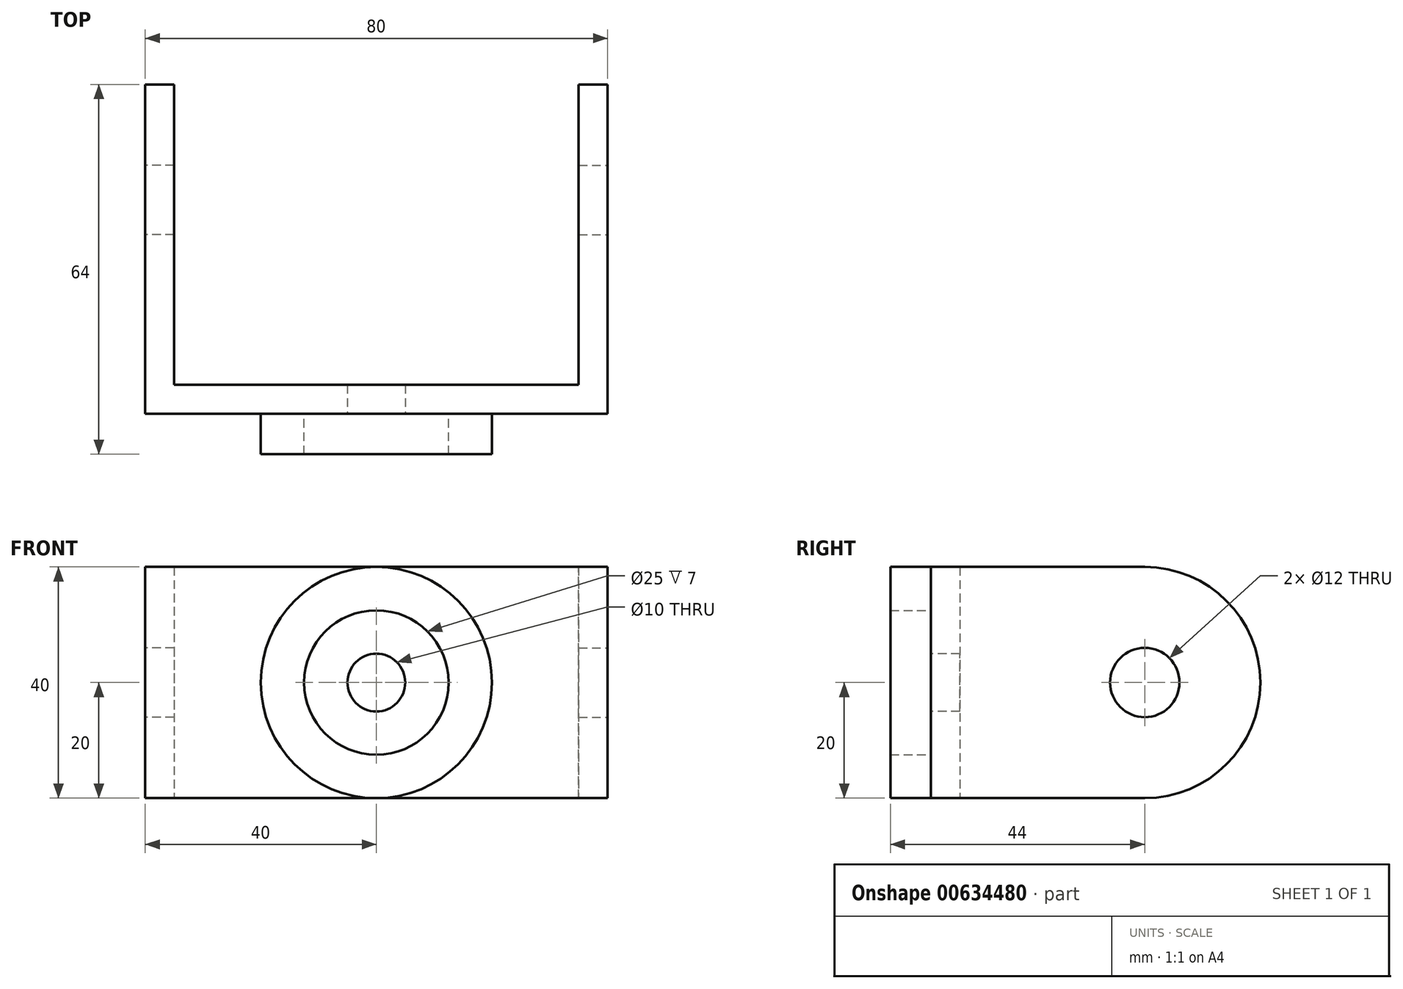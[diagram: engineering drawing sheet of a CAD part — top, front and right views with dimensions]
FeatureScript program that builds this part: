
annotation { "Feature Type Name" : "Feature", "Feature Type Description" : "" }
export const myFeature = defineFeature(function(context is Context, id is Id, definition is map)
    precondition{}
    {
        {
            var Q0;
            Q0=qCreatedBy(makeId("Front.planeOp"),FACE);
            var sketch = newSketch(context, id + "F0", { "sketchPlane" : qUnion([Q0])});
            skLineSegment(sketch, "E0.bottom", {"start": v(40, 20) * mm, "end": v(-40, 20) * mm});
            skLineSegment(sketch, "E0.top", {"start": v(40, -20) * mm, "end": v(-40, -20) * mm});
            skLineSegment(sketch, "E0.left", {"start": v(40, 20) * mm, "end": v(40, -20) * mm});
            skLineSegment(sketch, "E0.right", {"start": v(-40, 20) * mm, "end": v(-40, -20) * mm});
            skPoint(sketch, "E0.middle", {"position": v(0, 0) * mm});
            skCircle(sketch, "E1", {"center": v(0, 0) * mm, "radius": 5 * mm});
            skCircle(sketch, "E2", {"center": v(0, 0) * mm, "radius": 12.5 * mm});
            skCircle(sketch, "E3", {"center": v(0, 0) * mm, "radius": 20 * mm});
            skSolve(sketch);
        }
        {
            var Q0;
            Q0=makeQuery(id+"F0.imprint","IMPRINT",FACE,{"disambiguationData":[TD([[makeQuery(id+"F0.imprint","IMPRINT",EDGE,{"derivedFrom":sQuery(id+"F0.wireOp",EDGE,"E2")}),-1.0]])]});
            extrude(context, id + "F1", {"entities" : qUnion([Q0]), "depth" : 7 * mm, "offsetDistance" : 25 * mm});
        }
        {
            var Q0;
            {var subQ0=sQuery(id+"F0.wireOp",EDGE,"E0.right");Q0=makeQuery(id+"F0.imprint","IMPRINT",FACE,{"disambiguationData":[TD([[makeQuery(id+"F0.imprint","IMPRINT",EDGE,{"derivedFrom":subQ0}),1.0]])]});}
            var Q1;
            Q1=makeQuery(id+"F0.imprint","IMPRINT",FACE,{"disambiguationData":[TD([[makeQuery(id+"F0.imprint","IMPRINT",EDGE,{"derivedFrom":sQuery(id+"F0.wireOp",EDGE,"E2")}),-1.0]])]});
            var Q2;
            Q2=makeQuery(id+"F0.imprint","IMPRINT",FACE,{"disambiguationData":[TD([[makeQuery(id+"F0.imprint","IMPRINT",EDGE,{"derivedFrom":sQuery(id+"F0.wireOp",EDGE,"E1")}),-1.0]])]});
            var Q3;
            {var subQ0=sQuery(id+"F0.wireOp",EDGE,"E0.left");Q3=makeQuery(id+"F0.imprint","IMPRINT",FACE,{"disambiguationData":[TD([[makeQuery(id+"F0.imprint","IMPRINT",EDGE,{"derivedFrom":subQ0}),-1.0]])]});}
            extrude(context, id + "F2", {"entities" : qUnion([Q0, Q1, Q2, Q3]), "operationType" : NewBodyOperationType.ADD, "depth" : -5 * mm, "offsetDistance" : 25 * mm});
        }
        {
            var Q0;
            Q0=makeQuery(id+"F2.opExtrude","SWEPT_FACE",FACE,{"disambiguationData":[OSD([sQuery(id+"F0.wireOp",EDGE,"E0.left")])]});
            var sketch = newSketch(context, id + "F3", { "sketchPlane" : qUnion([Q0])});
            skLineSegment(sketch, "E4", {"start": v(0, -20) * mm, "end": v(37, -20) * mm});
            skPoint(sketch, "E5.endSnap0", {"position": v(2.5, 20) * mm});
            skLineSegment(sketch, "E6", {"start": v(37, 20) * mm, "end": v(0, 20) * mm});
            skLineSegment(sketch, "E7", {"start": v(0, 20) * mm, "end": v(0, -20) * mm});
            skCircle(sketch, "E8", {"center": v(37, 0) * mm, "radius": 6 * mm});
            skArc(sketch, "E9", {"start": v(37, -20) * mm, "mid": v(57, 0) * mm, "end": v(37, 20) * mm});
            skSolve(sketch);
        }
        {
            var Q0;
            Q0=makeQuery(id+"F3.imprint","IMPRINT",FACE,{"disambiguationData":[TD([[makeQuery(id+"F3.imprint","IMPRINT",EDGE,{"derivedFrom":sQuery(id+"F3.wireOp",EDGE,"E8")}),-1.0]])]});
            extrude(context, id + "F4", {"entities" : qUnion([Q0]), "operationType" : NewBodyOperationType.ADD, "depth" : -5 * mm, "offsetDistance" : 25 * mm});
        }
        {
            var Q0;
            Q0=makeQuery(id+"F2.opExtrude","SWEPT_FACE",FACE,{"disambiguationData":[OSD([sQuery(id+"F0.wireOp",EDGE,"E0.right")])]});
            var sketch = newSketch(context, id + "F5", { "sketchPlane" : qUnion([Q0])});
            skLineSegment(sketch, "E10", {"start": v(0, 20) * mm, "end": v(-37, 20) * mm});
            skLineSegment(sketch, "E11", {"start": v(-37, -20) * mm, "end": v(0, -20) * mm});
            skLineSegment(sketch, "E12", {"start": v(0, -20) * mm, "end": v(0, 20) * mm});
            skCircle(sketch, "E13", {"center": v(-37, 0) * mm, "radius": 6 * mm});
            skArc(sketch, "E14", {"start": v(-37, 20) * mm, "mid": v(-57, 0) * mm, "end": v(-37, -20) * mm});
            skSolve(sketch);
        }
        {
            var Q0;
            Q0=makeQuery(id+"F5.imprint","IMPRINT",FACE,{"disambiguationData":[TD([[makeQuery(id+"F5.imprint","IMPRINT",EDGE,{"derivedFrom":sQuery(id+"F5.wireOp",EDGE,"E13")}),-1.0]])]});
            extrude(context, id + "F6", {"entities" : qUnion([Q0]), "operationType" : NewBodyOperationType.ADD, "depth" : -5 * mm, "offsetDistance" : 25 * mm});
        }
    });
